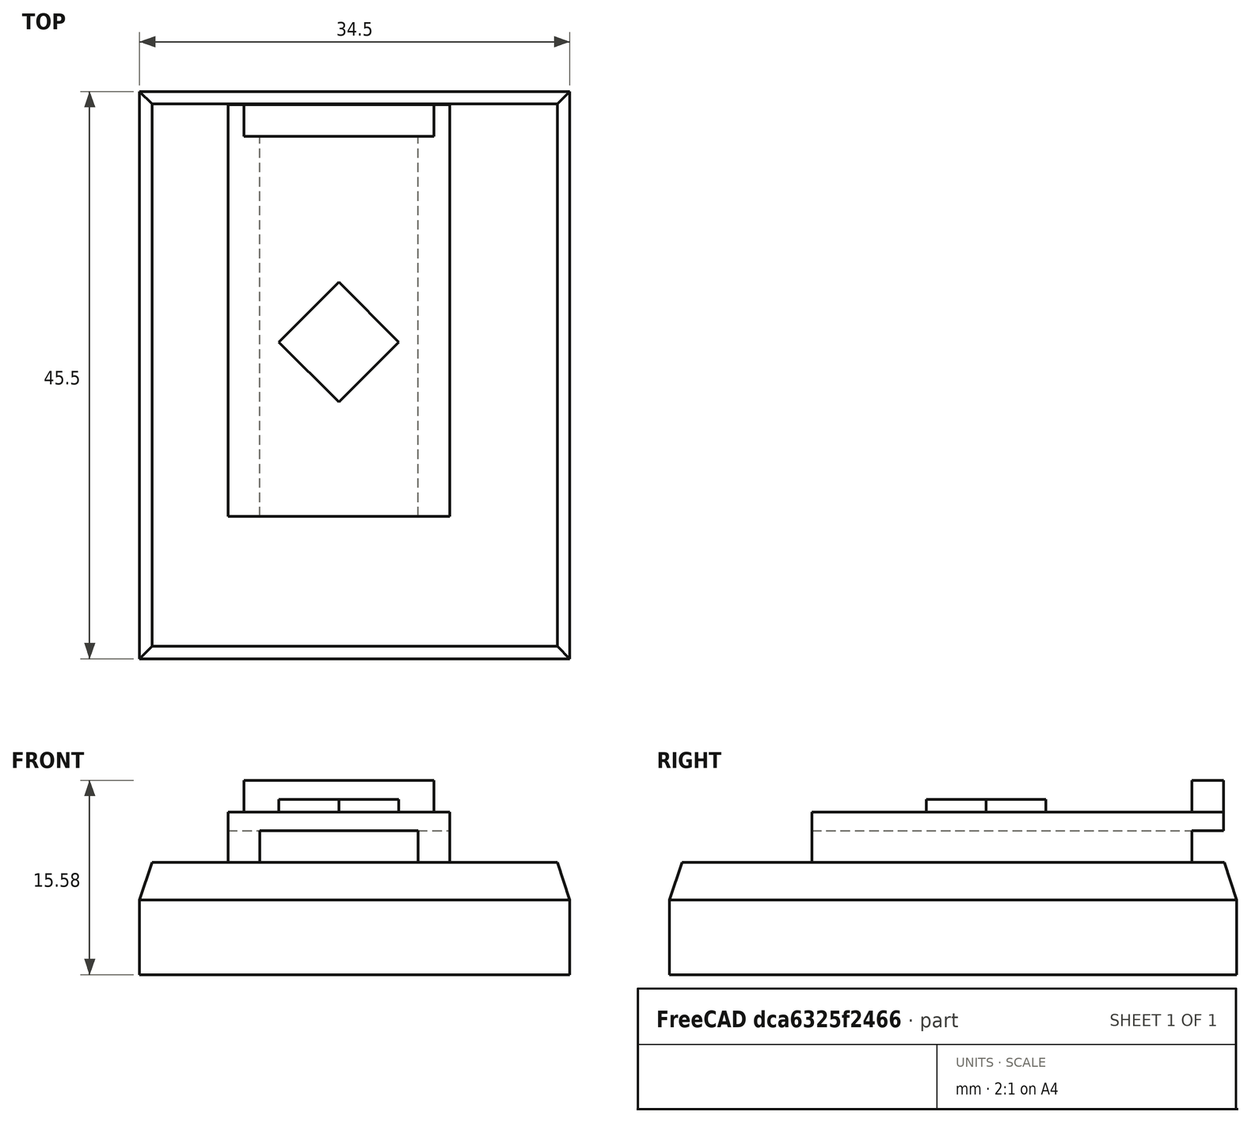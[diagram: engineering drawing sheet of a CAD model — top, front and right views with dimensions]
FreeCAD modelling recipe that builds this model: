
FCSTD DOCUMENT  (FreeCAD 0.14R3692 (Git))
Label: Board_ArduinoProMini
License: CC-BY 3.0
LicenseURL: http://creativecommons.org/licenses/by/3.0/
objects: Part::Box×5, App::DocumentObjectGroup×2, Part::MultiFuse×2, Part::Chamfer×1, Part::Feature×1
note: 9 computed .brp shape members not serialized (recipe doc carries the construction recipe); baked Part::Feature solids carry a one-line shape summary decoded from their .brp

FEATURE [Part::Box] Box  label="BreadBoard_Body"
  Height = 9
  Length = 34.5
  Width = 45.5
FEATURE [Part::Chamfer] Chamfer  label="BreadBoard_Chamfer"
  Base = -> Box
  Edges = 4 edges: [Edge2 r1=3 r2=1,Edge6 r1=3 r2=1,Edge10 r1=3 r2=1,Edge12 r1=3 r2=1]
FEATURE [App::DocumentObjectGroup] Grupo  label="BreadBoard_Group"
  Group = -> [Chamfer]
FEATURE [Part::Box] Box001  label="ArduinoProMini_PCB"
  Height = 1.5
  Length = 17.78
  Width = 33.02
FEATURE [Part::Box] Box002  label="ArduinoProMini_ATmega"
  Height = 1
  Length = 6.8
  Placement = pos=(8.89,9.16167,1.5) rot=(0,0,1;0.785398rad)
  Width = 6.8
FEATURE [Part::Box] Box003  label="ArduinoProMini_PinHeader12Right"
  Height = 2.54
  Length = 2.54
  Placement = pos=(0,0,-2.54) rot=(0,0,1;0rad)
  Width = 30.48
FEATURE [Part::Feature] Box003001  label="ArduinoProMini_PinHeader12Left"
  Placement = pos=(15.24,0,-2.54) rot=(0,0,1;0rad)
  shape: bbox 2.54 x 30.48 x 2.54 mm, 6 faces (baked)
FEATURE [Part::Box] Box003002  label="ArduinoProMini_PinHeader6"
  Height = 2.54
  Length = 15.24
  Placement = pos=(1.27,30.48,1.5) rot=(0,0,1;0rad)
  Width = 2.54
FEATURE [Part::MultiFuse] Fusion  label="ArduinoProMini"
  Placement = pos=(7.09,11.43,11.54) rot=(0,0,1;0rad)
  Shapes = -> [Box001,Box003001,Box003002,Box002,Box003]
FEATURE [App::DocumentObjectGroup] Grupo001  label="ArduinoProMini_Group"
  Group = -> [Box001,Box002,Box003,Box003001,Box003002,Fusion]
FEATURE [Part::MultiFuse] Fusion001  label="Board_ArduinoProMini"
  Placement = pos=(-17.25,0,0) rot=(0,0,1;0rad)
  Shapes = -> [Chamfer,Fusion]
